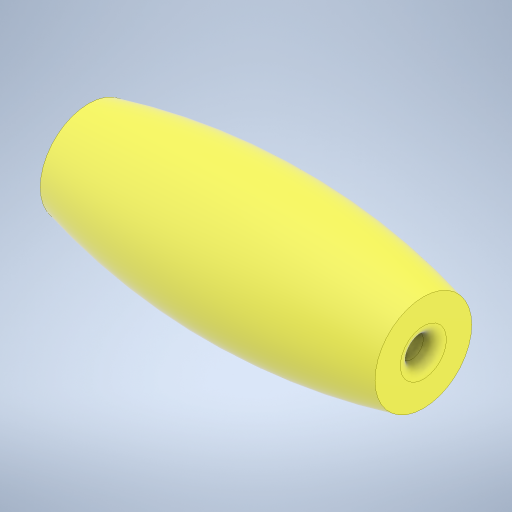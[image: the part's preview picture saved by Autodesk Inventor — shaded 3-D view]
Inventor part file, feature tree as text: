
AUTODESK INVENTOR PART (.ipt)
format: ipt  version: 2024.2 (Build 282272000, 272)  size: 286,720 bytes
history: native  units: mm
features: fillet x2, sketch x2, revolve x1, hole x1
ambient origin geometry x8: Origin, YZ Plane, XZ Plane, XY Plane, X Axis, Y Axis, Z Axis, Center Point
bodies: Solid1 (feature_tree)
feature tree (6):
  revolve  "Revolution1"  [1 undecoded]
  hole  "Hole1"  [1 undecoded]
  fillet  "Fillet1"  Radius=1.0mm
  fillet  "Fillet2"  Radius=2.0mm
  sketch  "Sketch1"  dims[d0=12.0mm d1=29.0mm]
  sketch  "Sketch2"  dims[d2=59.0mm d3=90.0deg d4=2.0mm d5=6.0mm d6=4.0mm d7=2.0mm d8=90.0deg d9=8.0mm d10=20.594885mm d11=1.0mm d12=2.0mm]
note: 2 required parameter values undecoded (feature->parameter linkage not recoverable at this tier; creation-order binding heuristic only, values carry confidence <= 0.55)